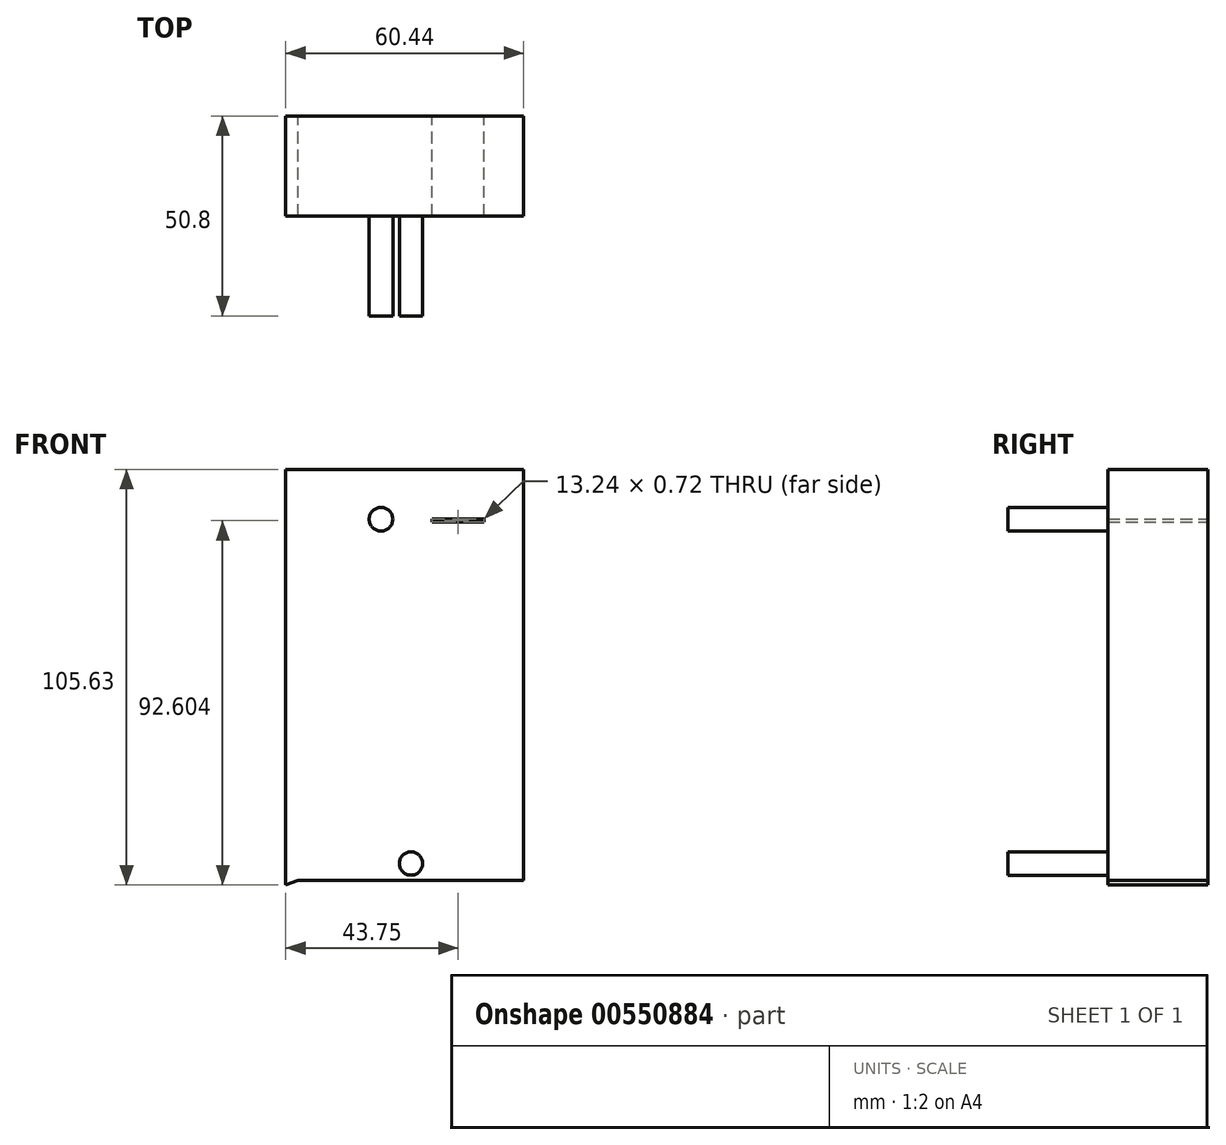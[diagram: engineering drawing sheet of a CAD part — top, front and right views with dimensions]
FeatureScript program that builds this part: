
annotation { "Feature Type Name" : "Feature", "Feature Type Description" : "" }
export const myFeature = defineFeature(function(context is Context, id is Id, definition is map)
    precondition{}
    {
        {
            var Q0;
            Q0=qCreatedBy(makeId("Front.planeOp"),FACE);
            var sketch = newSketch(context, id + "F0", { "sketchPlane" : qUnion([Q0])});
            skLineSegment(sketch, "E0.bottom", {"start": v(-31.37, 35.98) * mm, "end": v(25.9, 35.98) * mm});
            skLineSegment(sketch, "E0.top", {"start": v(-31.37, -64.76) * mm, "end": v(25.9, -64.76) * mm});
            skLineSegment(sketch, "E0.left", {"start": v(-31.37, 35.98) * mm, "end": v(-31.37, -64.76) * mm});
            skLineSegment(sketch, "E0.right", {"start": v(25.9, 35.98) * mm, "end": v(25.9, -64.76) * mm});
            skLineSegment(sketch, "E1.bottom", {"start": v(2.6, 27.05) * mm, "end": v(15.83, 27.05) * mm});
            skLineSegment(sketch, "E1.top", {"start": v(2.6, 26.33) * mm, "end": v(15.83, 26.33) * mm});
            skLineSegment(sketch, "E1.left", {"start": v(2.6, 27.05) * mm, "end": v(2.6, 26.33) * mm});
            skLineSegment(sketch, "E1.right", {"start": v(15.83, 27.05) * mm, "end": v(15.83, 26.33) * mm});
            skLineSegment(sketch, "E2.bottom", {"start": v(15.83, 27.05) * mm, "end": v(2.6, 27.05) * mm});
            skLineSegment(sketch, "E2.top", {"start": v(15.83, 27.05) * mm, "end": v(2.6, 27.05) * mm});
            skLineSegment(sketch, "E2.left", {"start": v(15.83, 27.05) * mm, "end": v(15.83, 27.05) * mm});
            skLineSegment(sketch, "E2.right", {"start": v(2.6, 27.05) * mm, "end": v(2.6, 27.05) * mm});
            skLineSegment(sketch, "E3", {"start": v(-31.37, 35.98) * mm, "end": v(-34.54, 39.72) * mm});
            skLineSegment(sketch, "E4", {"start": v(-34.54, 39.72) * mm, "end": v(25.9, 39.72) * mm});
            skLineSegment(sketch, "E5", {"start": v(25.9, 39.72) * mm, "end": v(25.9, 35.98) * mm});
            skLineSegment(sketch, "E6", {"start": v(-34.54, 39.72) * mm, "end": v(-34.54, -65.9) * mm});
            skLineSegment(sketch, "E7", {"start": v(-34.54, -65.9) * mm, "end": v(-31.37, -64.76) * mm});
            skLineSegment(sketch, "E8", {"start": v(-34.54, -65.9) * mm, "end": v(26.48, -65.9) * mm});
            skSolve(sketch);
        }
        {
            var Q0;
            Q0 = qSketchRegion(id + "F0", true);
            extrude(context, id + "F1", {"entities" : qUnion([Q0]), "depth" : 25.4 * mm, "offsetDistance" : 25.4 * mm});
        }
        {
            var Q0;
            Q0=makeQuery(id+"F1.opExtrude","CAP_FACE",FACE,{"disambiguationData":[OSD([sQuery(id+"F0.wireOp",EDGE,"E0.top"),sQuery(id+"F0.wireOp",EDGE,"E0.right"),sQuery(id+"F0.wireOp",EDGE,"E1.top"),sQuery(id+"F0.wireOp",EDGE,"E1.left"),sQuery(id+"F0.wireOp",EDGE,"E1.right"),sQuery(id+"F0.wireOp",EDGE,"E2.top"),sQuery(id+"F0.wireOp",EDGE,"E4"),sQuery(id+"F0.wireOp",EDGE,"E5"),sQuery(id+"F0.wireOp",EDGE,"E6"),sQuery(id+"F0.wireOp",EDGE,"E7")])],"isStart":false});
            var sketch = newSketch(context, id + "F2", { "sketchPlane" : qUnion([Q0])});
            skCircle(sketch, "E9", {"center": v(-10.36, 27.05) * mm, "radius": 3 * mm});
            skCircle(sketch, "E10", {"center": v(-2.73, -60.44) * mm, "radius": 2.97 * mm});
            skPoint(sketch, "E10.centerSnap0", {"position": v(-2.73, -64.76) * mm});
            skLineSegment(sketch, "E11", {"start": v(-34.54, -48.93) * mm, "end": v(25.9, -48.93) * mm});
            skLineSegment(sketch, "E12", {"start": v(-34.54, -46.05) * mm, "end": v(-34.54, 20.15) * mm});
            skLineSegment(sketch, "E13", {"start": v(-33.67, 20.72) * mm, "end": v(25.9, 20.72) * mm});
            skLineSegment(sketch, "E14", {"start": v(25.9, 20.72) * mm, "end": v(25.9, -48.93) * mm});
            skSolve(sketch);
        }
        {
            var Q0;
            Q0 = qSketchRegion(id + "F2", true);
            extrude(context, id + "F3", {"entities" : qUnion([Q0]), "operationType" : NewBodyOperationType.ADD, "depth" : 25.4 * mm, "offsetDistance" : 25.4 * mm});
        }
    });
